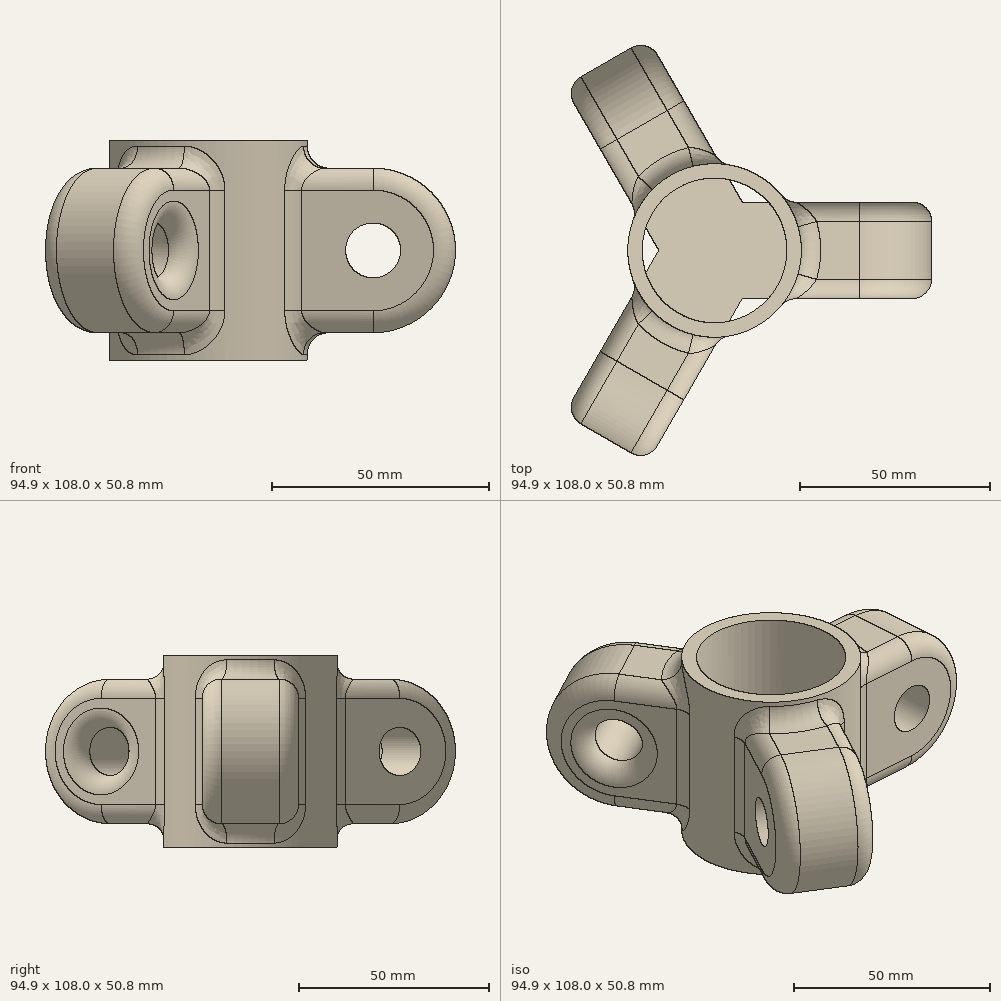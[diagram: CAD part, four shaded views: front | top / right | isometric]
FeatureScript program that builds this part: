
annotation { "Feature Type Name" : "Feature", "Feature Type Description" : "" }
export const myFeature = defineFeature(function(context is Context, id is Id, definition is map)
    precondition{}
    {
        {
            var Q0;
            Q0=qCreatedBy(makeId("Front.planeOp"),FACE);
            var sketch = newSketch(context, id + "F0", { "sketchPlane" : qUnion([Q0])});
            skCircle(sketch, "E0", {"center": v(38.1, 0) * mm, "radius": 6.35 * mm});
            skArc(sketch, "E1", {"start": v(38.1, -19.05) * mm, "mid": v(57.15, 0) * mm, "end": v(38.1, 19.05) * mm});
            skLineSegment(sketch, "E2.bottom", {"start": v(38.1, 19.05) * mm, "end": v(0, 19.05) * mm});
            skLineSegment(sketch, "E2.top", {"start": v(38.1, -19.05) * mm, "end": v(0, -19.05) * mm});
            skLineSegment(sketch, "E2.right", {"start": v(0, 19.05) * mm, "end": v(0, -19.05) * mm});
            skPoint(sketch, "E2.middle", {"position": v(19.05, 0) * mm});
            skSolve(sketch);
        }
        {
            var Q0;
            Q0 = qSketchRegion(id + "F0", true);
            extrude(context, id + "F1", {"entities" : qUnion([Q0]), "endBound" : BoundingType.SYMMETRIC, "depth" : 25.4 * mm});
        }
        {
            var Q0;
            Q0=makeQuery(id+"F1.opExtrude","CAP_EDGE",EDGE,{"disambiguationData":[OSD([sQuery(id+"F0.wireOp",EDGE,"E1")])],"isStart":false});
            var Q1;
            Q1=makeQuery(id+"F1.opExtrude","CAP_FACE",FACE,{"disambiguationData":[OSD([sQuery(id+"F0.wireOp",EDGE,"E0"),sQuery(id+"F0.wireOp",EDGE,"E1"),sQuery(id+"F0.wireOp",EDGE,"E2.bottom"),sQuery(id+"F0.wireOp",EDGE,"E2.top"),sQuery(id+"F0.wireOp",EDGE,"E2.right")])],"isStart":true});
            fillet(context, id + "F2", {"entities" : qUnion([Q0, Q1]), "radius" : 5.08 * mm, "tangentPropagation" : true, "allowEdgeOverflow" : false});
        }
        {
            var Q0;
            Q0=qCreatedBy(makeId("Top.planeOp"),FACE);
            var sketch = newSketch(context, id + "F3", { "sketchPlane" : qUnion([Q0])});
            skCircle(sketch, "E3", {"center": v(0, 0) * mm, "radius": 22.86 * mm});
            skCircle(sketch, "E4", {"center": v(0, 0) * mm, "radius": 19.05 * mm});
            skSolve(sketch);
        }
        {
            var Q0;
            Q0=makeQuery(id+"F1.opExtrude","SWEPT_BODY",BODY,{"disambiguationData":[OSD([sQuery(id+"F0.wireOp",EDGE,"E0"),sQuery(id+"F0.wireOp",EDGE,"E1"),sQuery(id+"F0.wireOp",EDGE,"E2.bottom"),sQuery(id+"F0.wireOp",EDGE,"E2.top"),sQuery(id+"F0.wireOp",EDGE,"E2.right")])]});
            var Q1;
            Q1=sQuery(id+"F3.wireOp",EDGE,"E4");
            circularPattern(context, id + "F4", {"entities" : qUnion([Q0]), "axis" : qUnion([Q1]), "angle" : 360 * degree, "instanceCount" : 3, "equalSpace" : true});
        }
        {
            var Q0;
            Q0 = qSketchRegion(id + "F3", true);
            extrude(context, id + "F5", {"entities" : qUnion([Q0]), "operationType" : NewBodyOperationType.ADD, "endBound" : BoundingType.SYMMETRIC, "depth" : 50.8 * mm});
        }
        {
            var Q0;
            {var subQ0=makeQuery(id+"F1.opExtrude","SWEPT_FACE",FACE,{"disambiguationData":[OSD([sQuery(id+"F0.wireOp",EDGE,"E2.bottom")])]});Q0=makeQuery(id+"F5.boolean.opBoolean","MERGE",FACE,{"derivedFrom":[subQ0,makeQuery(id+"F4.opPattern","COPY",FACE,{"derivedFrom":subQ0,"instanceName":"1"}),makeQuery(id+"F4.opPattern","COPY",FACE,{"derivedFrom":subQ0,"instanceName":"2"}),makeQuery(id+"F5.opExtrude","CAP_FACE",FACE,{"disambiguationData":[OSD([sQuery(id+"F3.wireOp",EDGE,"E3"),sQuery(id+"F3.wireOp",EDGE,"E4")])],"isStart":false})]});}
            var sketch = newSketch(context, id + "F6", { "sketchPlane" : qUnion([Q0])});
            skCircle(sketch, "E5", {"center": v(0, 0) * mm, "radius": 19.05 * mm});
            skSolve(sketch);
        }
        {
            var Q0;
            Q0 = qSketchRegion(id + "F6", true);
            extrude(context, id + "F7", {"entities" : qUnion([Q0]), "operationType" : NewBodyOperationType.REMOVE, "oppositeDirection" : true, "depth" : 25.4 * mm});
        }
        {
            var Q0;
            {var subQ0=sQuery(id+"F0.wireOp",EDGE,"E2.bottom");Q0=makeQuery(id+"F5.boolean.opBoolean","INTERSECT",EDGE,{"derivedFrom":[makeQuery(id+"F2.opFillet","BLEND_FACE",FACE,{"disambiguationData":[OSD([subQ0]),TDD([makeQuery(id+"F1.opExtrude","CAP_EDGE",EDGE,{"disambiguationData":[OSD([subQ0])],"isStart":true})])]}),makeQuery(id+"F5.opExtrude","SWEPT_FACE",FACE,{"disambiguationData":[OSD([sQuery(id+"F3.wireOp",EDGE,"E3")])]})]});}
            var Q1;
            {var subQ0=sQuery(id+"F0.wireOp",EDGE,"E2.bottom");Q1=makeQuery(id+"F5.boolean.opBoolean","INTERSECT",EDGE,{"derivedFrom":[makeQuery(id+"F4.opPattern","COPY",FACE,{"derivedFrom":makeQuery(id+"F2.opFillet","BLEND_FACE",FACE,{"disambiguationData":[OSD([subQ0]),TDD([makeQuery(id+"F1.opExtrude","CAP_EDGE",EDGE,{"disambiguationData":[OSD([subQ0])],"isStart":false})])]}),"instanceName":"1"}),makeQuery(id+"F5.opExtrude","SWEPT_FACE",FACE,{"disambiguationData":[OSD([sQuery(id+"F3.wireOp",EDGE,"E3")])]})]});}
            var Q2;
            Q2=makeQuery(id+"F5.boolean.opBoolean","INTERSECT",EDGE,{"derivedFrom":[makeQuery(id+"F4.opPattern","COPY",FACE,{"derivedFrom":makeQuery(id+"F1.opExtrude","CAP_FACE",FACE,{"disambiguationData":[OSD([sQuery(id+"F0.wireOp",EDGE,"E0"),sQuery(id+"F0.wireOp",EDGE,"E1"),sQuery(id+"F0.wireOp",EDGE,"E2.bottom"),sQuery(id+"F0.wireOp",EDGE,"E2.top"),sQuery(id+"F0.wireOp",EDGE,"E2.right")])],"isStart":false}),"instanceName":"2"}),makeQuery(id+"F5.opExtrude","SWEPT_FACE",FACE,{"disambiguationData":[OSD([sQuery(id+"F3.wireOp",EDGE,"E3")])]})]});
            var Q3;
            Q3=makeQuery(id+"F5.boolean.opBoolean","INTERSECT",EDGE,{"derivedFrom":[makeQuery(id+"F4.opPattern","COPY",FACE,{"derivedFrom":makeQuery(id+"F1.opExtrude","CAP_FACE",FACE,{"disambiguationData":[OSD([sQuery(id+"F0.wireOp",EDGE,"E0"),sQuery(id+"F0.wireOp",EDGE,"E1"),sQuery(id+"F0.wireOp",EDGE,"E2.bottom"),sQuery(id+"F0.wireOp",EDGE,"E2.top"),sQuery(id+"F0.wireOp",EDGE,"E2.right")])],"isStart":true}),"instanceName":"1"}),makeQuery(id+"F5.opExtrude","SWEPT_FACE",FACE,{"disambiguationData":[OSD([sQuery(id+"F3.wireOp",EDGE,"E3")])]})]});
            var Q4;
            Q4=makeQuery(id+"F5.boolean.opBoolean","INTERSECT",EDGE,{"derivedFrom":[makeQuery(id+"F4.opPattern","COPY",FACE,{"derivedFrom":makeQuery(id+"F1.opExtrude","CAP_FACE",FACE,{"disambiguationData":[OSD([sQuery(id+"F0.wireOp",EDGE,"E0"),sQuery(id+"F0.wireOp",EDGE,"E1"),sQuery(id+"F0.wireOp",EDGE,"E2.bottom"),sQuery(id+"F0.wireOp",EDGE,"E2.top"),sQuery(id+"F0.wireOp",EDGE,"E2.right")])],"isStart":true}),"instanceName":"2"}),makeQuery(id+"F5.opExtrude","SWEPT_FACE",FACE,{"disambiguationData":[OSD([sQuery(id+"F3.wireOp",EDGE,"E3")])]})]});
            var Q5;
            Q5=makeQuery(id+"F5.boolean.opBoolean","INTERSECT",EDGE,{"derivedFrom":[makeQuery(id+"F1.opExtrude","CAP_FACE",FACE,{"disambiguationData":[OSD([sQuery(id+"F0.wireOp",EDGE,"E0"),sQuery(id+"F0.wireOp",EDGE,"E1"),sQuery(id+"F0.wireOp",EDGE,"E2.bottom"),sQuery(id+"F0.wireOp",EDGE,"E2.top"),sQuery(id+"F0.wireOp",EDGE,"E2.right")])],"isStart":false}),makeQuery(id+"F5.opExtrude","SWEPT_FACE",FACE,{"disambiguationData":[OSD([sQuery(id+"F3.wireOp",EDGE,"E3")])]})]});
            fillet(context, id + "F8", {"entities" : qUnion([Q0, Q1, Q2, Q3, Q4, Q5]), "radius" : 5.08 * mm, "tangentPropagation" : true, "allowEdgeOverflow" : false});
        }
    });
